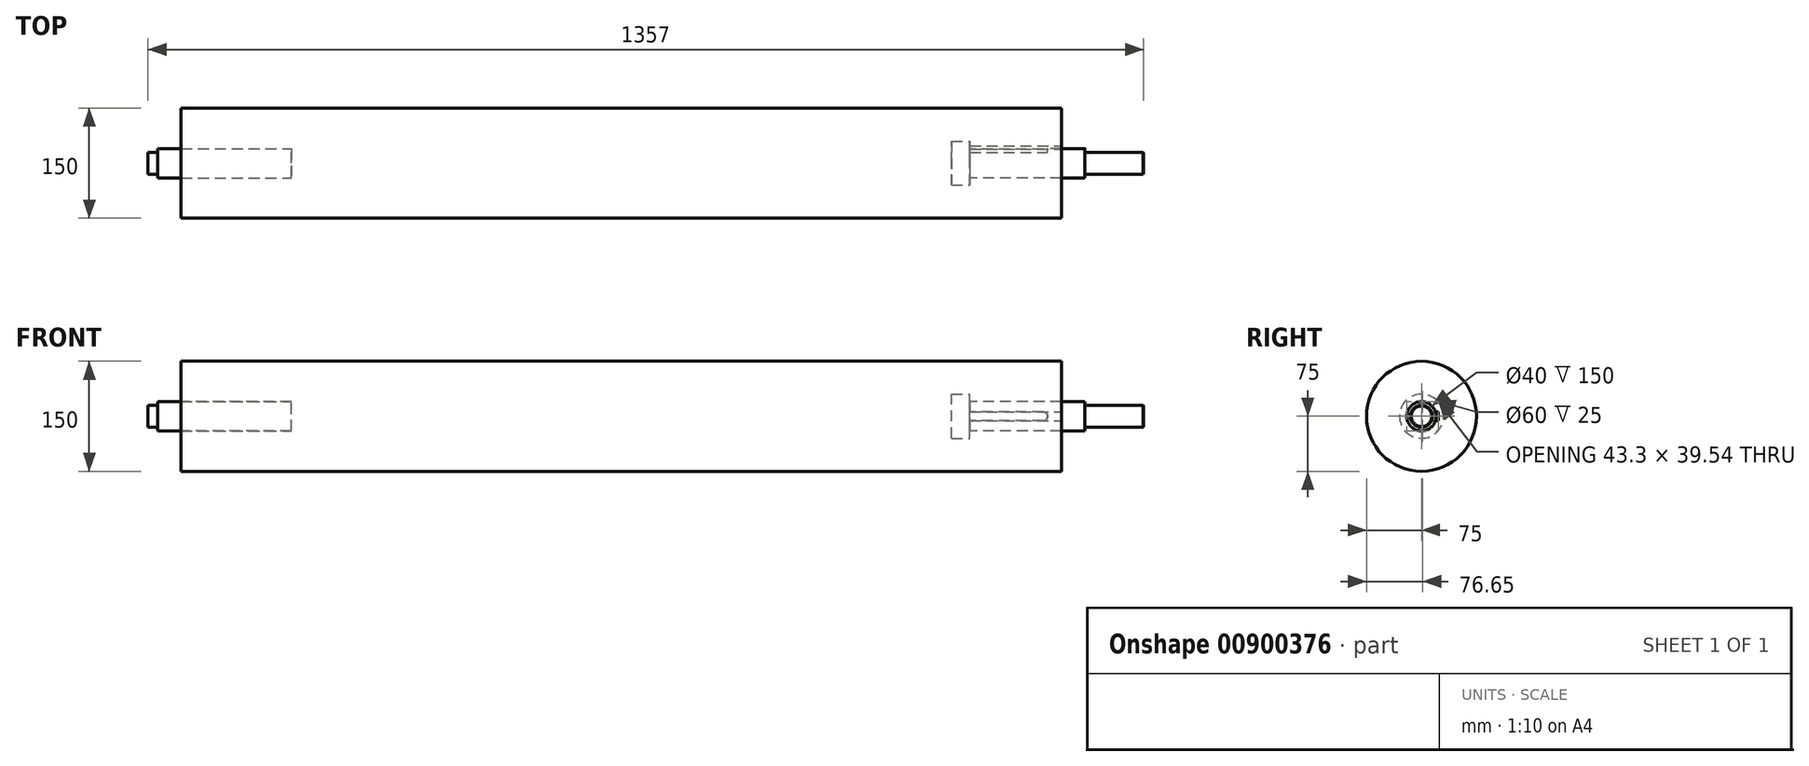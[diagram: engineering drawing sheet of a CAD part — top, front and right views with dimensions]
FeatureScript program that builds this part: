
annotation { "Feature Type Name" : "Feature", "Feature Type Description" : "" }
export const myFeature = defineFeature(function(context is Context, id is Id, definition is map)
    precondition{}
    {
        {
            var Q0;
            Q0=qCreatedBy(makeId("Right.planeOp"),FACE);
            var sketch = newSketch(context, id + "F0", { "sketchPlane" : qUnion([Q0])});
            skCircle(sketch, "E0", {"center": v(0, 0) * mm, "radius": 75 * mm});
            skSolve(sketch);
        }
        {
            var Q0;
            Q0=qSketchRegion(id+"F0",true);
            extrude(context, id + "F1", {"entities" : qUnion([Q0]), "endBound" : BoundingType.SYMMETRIC, "depth" : 1200 * mm, "offsetDistance" : 25 * mm});
        }
        {
            var Q0;
            Q0=makeQuery(id+"F1.opExtrude","CAP_FACE",FACE,{"disambiguationData":[OSD([sQuery(id+"F0.wireOp",EDGE,"E0")])],"isStart":false});
            var sketch = newSketch(context, id + "F2", { "sketchPlane" : qUnion([Q0])});
            skCircle(sketch, "E1", {"center": v(0, 0) * mm, "radius": 20 * mm});
            skSolve(sketch);
        }
        {
            var Q0;
            Q0=qSketchRegion(id+"F2",true);
            extrude(context, id + "F3", {"entities" : qUnion([Q0]), "operationType" : NewBodyOperationType.REMOVE, "oppositeDirection" : true, "depth" : 150 * mm, "offsetDistance" : 25 * mm});
        }
        {
            var Q0;
            Q0=makeQuery(id+"F1.opExtrude","CAP_FACE",FACE,{"disambiguationData":[OSD([sQuery(id+"F0.wireOp",EDGE,"E0")])],"isStart":true});
            var sketch = newSketch(context, id + "F4", { "sketchPlane" : qUnion([Q0])});
            skCircle(sketch, "E2", {"center": v(0, 0) * mm, "radius": 20 * mm});
            skSolve(sketch);
        }
        {
            var Q0;
            Q0=qSketchRegion(id+"F4",true);
            extrude(context, id + "F5", {"entities" : qUnion([Q0]), "operationType" : NewBodyOperationType.REMOVE, "oppositeDirection" : true, "depth" : 150 * mm, "offsetDistance" : 25 * mm});
        }
        {
            var Q0;
            Q0=makeQuery(id+"F1.opExtrude","CAP_FACE",FACE,{"disambiguationData":[OSD([sQuery(id+"F0.wireOp",EDGE,"E0")])],"isStart":false});
            var sketch = newSketch(context, id + "F6", { "sketchPlane" : qUnion([Q0])});
            skLineSegment(sketch, "E3.bottom", {"start": v(19.08, 6) * mm, "end": v(23.3, 6) * mm});
            skLineSegment(sketch, "E3.top", {"start": v(19.08, -6) * mm, "end": v(23.3, -6) * mm});
            skLineSegment(sketch, "E3.left", {"start": v(19.08, 6) * mm, "end": v(19.08, -6) * mm});
            skLineSegment(sketch, "E3.right", {"start": v(23.3, 6) * mm, "end": v(23.3, -6) * mm});
            skPoint(sketch, "E3.middle", {"position": v(21.19, 0) * mm});
            skSolve(sketch);
        }
        {
            var Q0;
            Q0=qSketchRegion(id+"F6",true);
            extrude(context, id + "F7", {"entities" : qUnion([Q0]), "operationType" : NewBodyOperationType.REMOVE, "oppositeDirection" : true, "depth" : 125 * mm, "offsetDistance" : 25 * mm});
        }
        {
            var Q0;
            Q0=makeQuery(id+"F3.boolean.opBoolean","COPY",FACE,{"derivedFrom":makeQuery(id+"F3.opExtrude","CAP_FACE",FACE,{"disambiguationData":[OSD([sQuery(id+"F2.wireOp",EDGE,"E1")])],"isStart":false})});
            var sketch = newSketch(context, id + "F8", { "sketchPlane" : qUnion([Q0])});
            skCircle(sketch, "E4", {"center": v(0, 0) * mm, "radius": 20 * mm});
            skSolve(sketch);
        }
        {
            var Q0;
            Q0=qSketchRegion(id+"F8",true);
            extrude(context, id + "F9", {"entities" : qUnion([Q0]), "depth" : 182 * mm, "offsetDistance" : 25 * mm});
        }
        {
            var Q0;
            Q0=makeQuery(id+"F9.opExtrude","CAP_FACE",FACE,{"disambiguationData":[OSD([sQuery(id+"F8.wireOp",EDGE,"E4")])],"isStart":false});
            var sketch = newSketch(context, id + "F10", { "sketchPlane" : qUnion([Q0])});
            skCircle(sketch, "E5", {"center": v(0, 0) * mm, "radius": 15 * mm});
            skSolve(sketch);
        }
        {
            var Q0;
            Q0=qSketchRegion(id+"F10",true);
            extrude(context, id + "F11", {"entities" : qUnion([Q0]), "operationType" : NewBodyOperationType.ADD, "depth" : 80 * mm, "offsetDistance" : 25 * mm});
        }
        {
            var Q0;
            Q0=makeQuery(id+"F9.opExtrude","SWEPT_BODY",BODY,{"disambiguationData":[OSD([sQuery(id+"F8.wireOp",EDGE,"E4")])]});
            var Q1;
            Q1=qCreatedBy(makeId("Right.planeOp"),FACE);
            mirror(context, id + "F12", {"entities" : qUnion([Q0]), "mirrorPlane" : qUnion([Q1])});
        }
        {
            var Q0;
            Q0=makeQuery(id+"F7.boolean.opBoolean","COPY",FACE,{"derivedFrom":makeQuery(id+"F7.opExtrude","SWEPT_FACE",FACE,{"disambiguationData":[OSD([sQuery(id+"F6.wireOp",EDGE,"E3.right")])]})});
            var sketch = newSketch(context, id + "F13", { "sketchPlane" : qUnion([Q0])});
            skLineSegment(sketch, "E6", {"start": v(475, 0) * mm, "end": v(575, 0) * mm});
            skArc(sketch, "E7.0.startCap", {"start": v(475, -6) * mm, "mid": v(469, 0) * mm, "end": v(475, 6) * mm});
            skArc(sketch, "E7.0.endCap", {"start": v(575, 6) * mm, "mid": v(581, 0) * mm, "end": v(575, -6) * mm});
            skLineSegment(sketch, "E7.0.left", {"start": v(475, 6) * mm, "end": v(575, 6) * mm});
            skLineSegment(sketch, "E7.0.right", {"start": v(475, -6) * mm, "end": v(575, -6) * mm});
            skSolve(sketch);
        }
        {
            var Q0;
            Q0=qSketchRegion(id+"F13",true);
            extrude(context, id + "F14", {"entities" : qUnion([Q0]), "operationType" : NewBodyOperationType.REMOVE, "depth" : 8.8 * mm, "offsetDistance" : 25 * mm});
        }
        {
            var Q0;
            Q0=makeQuery(id+"F1.opExtrude","CAP_FACE",FACE,{"disambiguationData":[OSD([sQuery(id+"F0.wireOp",EDGE,"E0")])],"isStart":false});
            cPlane(context, id + "F15", {"entities" : qUnion([Q0]), "cplaneType" : CPlaneType.OFFSET, "offset" : 125 * mm, "oppositeDirection" : true, "width" : 150 * mm, "height" : 150 * mm});
        }
        {
            var Q0;
            Q0=qCreatedBy(id+"F15.planeOp",FACE);
            var sketch = newSketch(context, id + "F16", { "sketchPlane" : qUnion([Q0])});
            skCircle(sketch, "E8", {"center": v(0, 0) * mm, "radius": 30 * mm});
            skSolve(sketch);
        }
        {
            var Q0;
            Q0 = qSketchRegion(id + "F16", true);
            extrude(context, id + "F17", {"entities" : qUnion([Q0]), "operationType" : NewBodyOperationType.REMOVE, "oppositeDirection" : true, "depth" : 25 * mm, "offsetDistance" : 25 * mm});
        }
        {
            var Q0;
            Q0=makeQuery(id+"F12.opPattern","COPY",FACE,{"derivedFrom":makeQuery(id+"F11.opExtrude","CAP_FACE",FACE,{"disambiguationData":[OSD([sQuery(id+"F10.wireOp",EDGE,"E5")])],"isStart":false}),"instanceName":"1"});
            extrude(context, id + "F18", {"entities" : qUnion([Q0]), "operationType" : NewBodyOperationType.REMOVE, "oppositeDirection" : true, "depth" : 67 * mm, "offsetDistance" : 25 * mm});
        }
        {
            var Q0;
            Q0=makeQuery(id+"F18.boolean.opBoolean","COPY",EDGE,{"derivedFrom":makeQuery(id+"F18.opExtrude","CAP_EDGE",EDGE,{"disambiguationData":[OSD([sQuery(id+"F10.wireOp",EDGE,"E5")])],"isStart":false})});
            var Q1;
            Q1=makeQuery(id+"F11.opExtrude","CAP_EDGE",EDGE,{"disambiguationData":[OSD([sQuery(id+"F10.wireOp",EDGE,"E5")])],"isStart":false});
            chamfer(context, id + "F19", {"entities" : qUnion([Q0, Q1]), "width" : 1 * mm, "tangentPropagation" : true});
        }
    });
